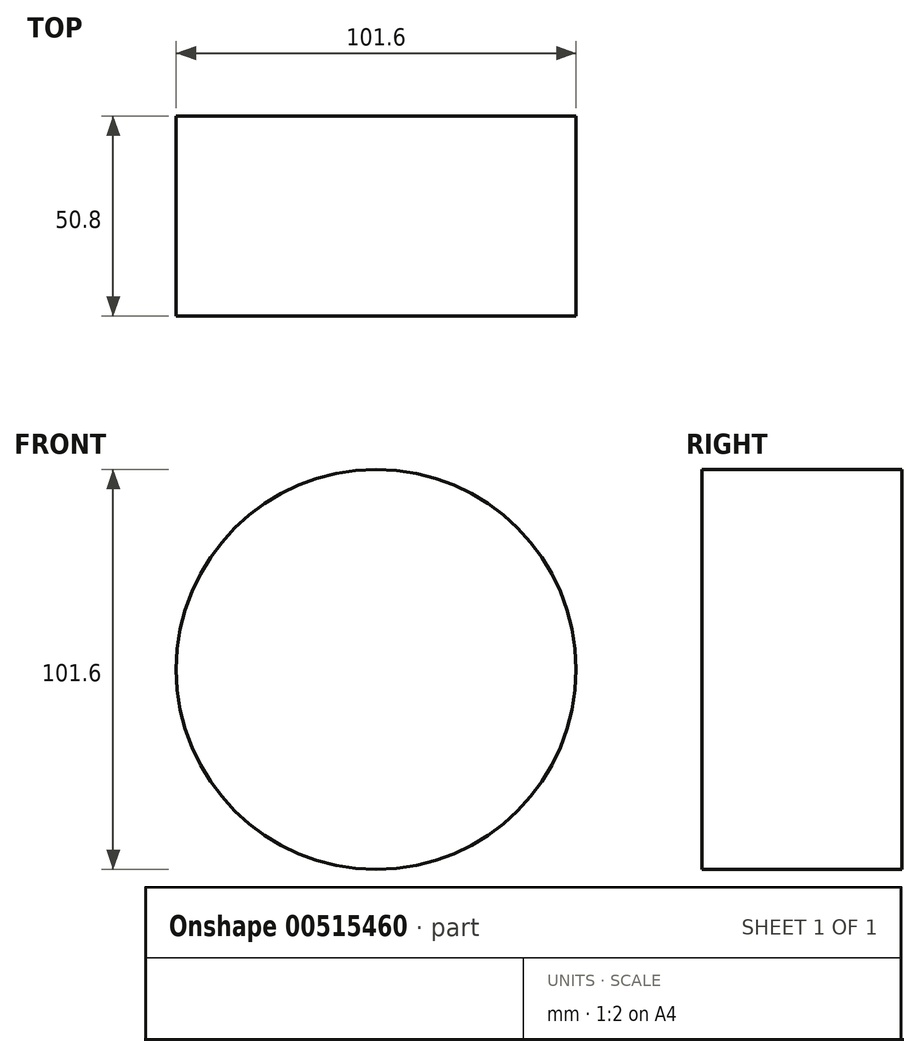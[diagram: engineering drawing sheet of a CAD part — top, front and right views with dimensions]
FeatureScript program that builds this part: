
annotation { "Feature Type Name" : "Feature", "Feature Type Description" : "" }
export const myFeature = defineFeature(function(context is Context, id is Id, definition is map)
    precondition{}
    {
        {
            var Q0;
            Q0=qCreatedBy(makeId("Front.planeOp"),FACE);
            var sketch = newSketch(context, id + "F0", { "sketchPlane" : qUnion([Q0])});
            skCircle(sketch, "E0", {"center": v(0, 0) * mm, "radius": 50.8 * mm});
            skSolve(sketch);
        }
        {
            var Q0;
            Q0 = qSketchRegion(id + "F0", true);
            extrude(context, id + "F1", {"entities" : qUnion([Q0]), "depth" : 50.8 * mm, "offsetDistance" : 25.4 * mm});
        }
    });
